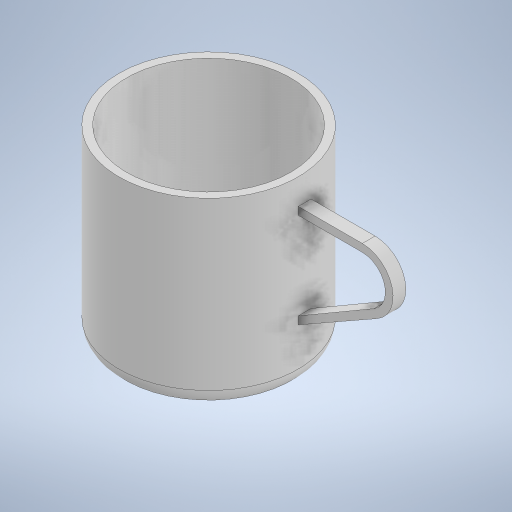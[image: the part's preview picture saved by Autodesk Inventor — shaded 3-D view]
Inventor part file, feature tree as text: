
AUTODESK INVENTOR PART (.ipt)
format: ipt  version: 2024 (Build 280153000, 153)  size: 279,040 bytes
history: native  units: mm
features: sketch x4, other x2, plane x2, extrude x2, revolve x1, shell x1
ambient origin geometry x8: Origin, YZ Plane, XZ Plane, XY Plane, X Axis, Y Axis, Z Axis, Center Point
bodies: Body1 (feature_tree)
feature tree (12):
  other  "Sección transversal1"
  other  "Sólido1"
  revolve  "Revolución1"  [1 undecoded]
  shell  "Vaciado2"  Thickness=10.0mm
  sketch  "Boceto2"  dims[d7=0.5mm d8=2.0mm d9=0.0mm d10=20.0mm d11=10.0mm]
  plane  "Plano de trabajo7"
  plane  "Plano de trabajo8"
  extrude  "Extrusión1"  Depth=15.0mm
  sketch  "Boceto5"  dims[d12=25.0mm d13=15.0mm]
  extrude  "Extrusión2"  Depth=5.0mm TaperAngle=0.0deg
  sketch  "Boceto1"  dims[d4=360.0deg d6=3.0mm]
  sketch  "Boceto6"  dims[d20=12.0mm d21=5.0mm d22=0.0mm d23=3.0mm d24=3.0mm d26=3.0mm d27=3.0mm d28=3.0mm d29=25.0mm d30=9.0mm d31=5.0mm d32=0.0mm]
note: 1 required parameter value undecoded (feature->parameter linkage not recoverable at this tier; creation-order binding heuristic only, values carry confidence <= 0.55)
